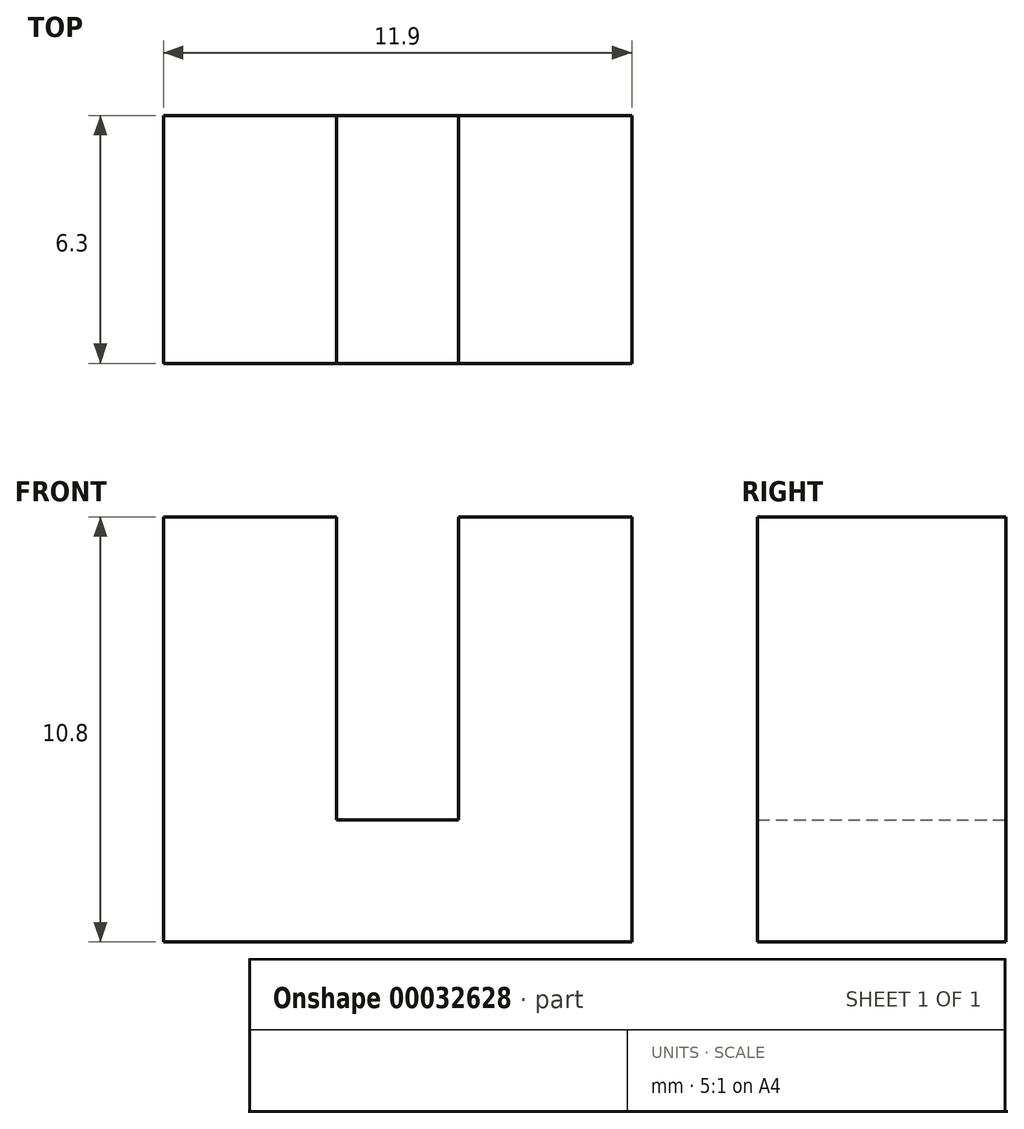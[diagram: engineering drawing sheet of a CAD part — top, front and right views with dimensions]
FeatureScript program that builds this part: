
annotation { "Feature Type Name" : "Feature", "Feature Type Description" : "" }
export const myFeature = defineFeature(function(context is Context, id is Id, definition is map)
    precondition{}
    {
        {
            var Q0;
            Q0=qCreatedBy(makeId("Front.planeOp"),FACE);
            var sketch = newSketch(context, id + "F0", { "sketchPlane" : qUnion([Q0])});
            skLineSegment(sketch, "E0", {"start": v(1.55, -0.5) * mm, "end": v(-1.55, -0.5) * mm});
            skLineSegment(sketch, "E1", {"start": v(-1.55, -0.5) * mm, "end": v(-1.55, 7.2) * mm});
            skLineSegment(sketch, "E2", {"start": v(-1.55, 7.2) * mm, "end": v(-5.95, 7.2) * mm});
            skLineSegment(sketch, "E3", {"start": v(-5.95, 7.2) * mm, "end": v(-5.95, -3.6) * mm});
            skLineSegment(sketch, "E4", {"start": v(-5.95, -3.6) * mm, "end": v(5.95, -3.6) * mm});
            skLineSegment(sketch, "E5", {"start": v(5.95, -3.6) * mm, "end": v(5.95, 7.2) * mm});
            skLineSegment(sketch, "E6", {"start": v(5.95, 7.2) * mm, "end": v(1.55, 7.2) * mm});
            skLineSegment(sketch, "E7", {"start": v(1.55, 7.2) * mm, "end": v(1.55, -0.5) * mm});
            skPoint(sketch, "E8", {"position": v(0, -0.5) * mm});
            skLineSegment(sketch, "E9", {"start": v(0, 0) * mm, "end": v(0, -11.73) * mm, "construction": true});
            skSolve(sketch);
        }
        {
            var Q0;
            Q0=makeQuery(id+"F0.imprint","IMPRINT",FACE,{"disambiguationData":[TD([[makeQuery(id+"F0.imprint","IMPRINT",EDGE,{"derivedFrom":sQuery(id+"F0.wireOp",EDGE,"E0")}),1.0]])]});
            extrude(context, id + "F1", {"entities" : qUnion([Q0]), "endBound" : BoundingType.SYMMETRIC, "depth" : 6.3 * mm});
        }
    });
